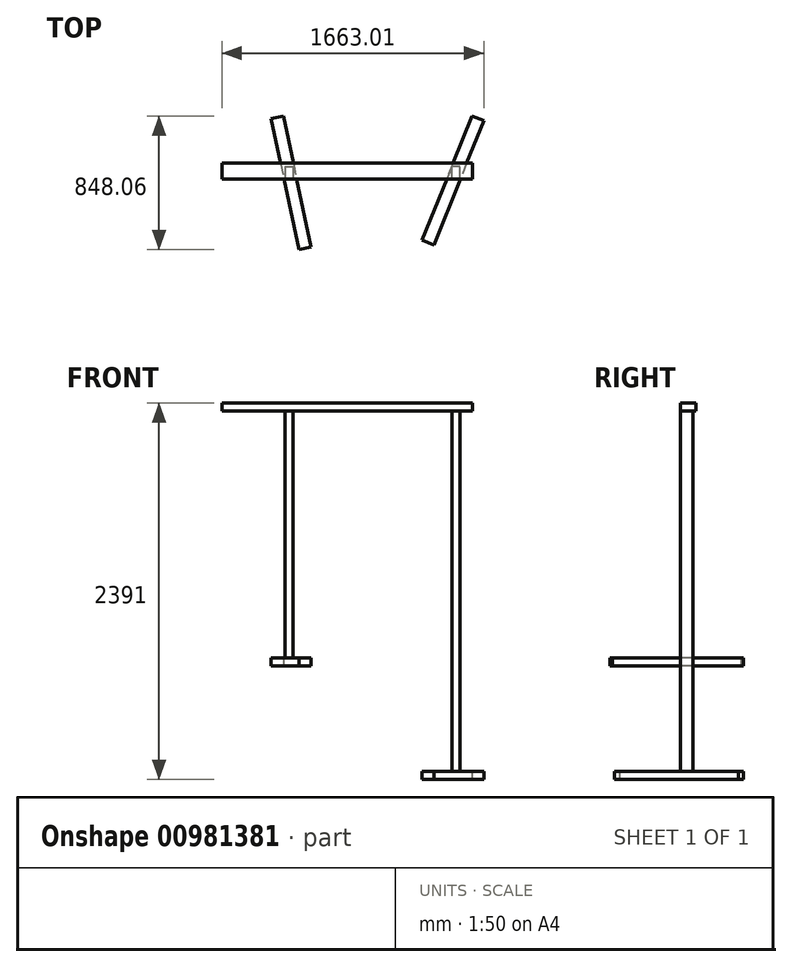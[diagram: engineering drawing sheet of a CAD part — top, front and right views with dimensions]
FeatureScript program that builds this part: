
annotation { "Feature Type Name" : "Feature", "Feature Type Description" : "" }
export const myFeature = defineFeature(function(context is Context, id is Id, definition is map)
    precondition{}
    {
        {
            var Q0;
            Q0=qCreatedBy(makeId("Top.planeOp"),FACE);
            var sketch = newSketch(context, id + "F0", { "sketchPlane" : qUnion([Q0])});
            skLineSegment(sketch, "E0.bottom", {"start": v(-104.92, 429.48) * mm, "end": v(-26.67, 446.11) * mm});
            skLineSegment(sketch, "E0.top", {"start": v(71.8, -401.95) * mm, "end": v(150.05, -385.31) * mm});
            skLineSegment(sketch, "E0.left", {"start": v(-104.92, 429.48) * mm, "end": v(71.8, -401.95) * mm});
            skLineSegment(sketch, "E0.right", {"start": v(-26.67, 446.11) * mm, "end": v(150.05, -385.31) * mm});
            skLineSegment(sketch, "E1.bottom", {"start": v(1173.33, 446.11) * mm, "end": v(1247.5, 416.14) * mm});
            skLineSegment(sketch, "E1.top", {"start": v(854.91, -342) * mm, "end": v(929.09, -371.96) * mm});
            skLineSegment(sketch, "E1.left", {"start": v(1173.33, 446.11) * mm, "end": v(854.91, -342) * mm});
            skLineSegment(sketch, "E1.right", {"start": v(1247.5, 416.14) * mm, "end": v(929.09, -371.96) * mm});
            skSolve(sketch);
        }
        {
            var Q0;
            Q0=makeQuery(id+"F0.imprint","IMPRINT",FACE,{"disambiguationData":[TD([[makeQuery(id+"F0.imprint","IMPRINT",EDGE,{"derivedFrom":sQuery(id+"F0.wireOp",EDGE,"E0.bottom")}),-1.0]])]});
            var Q1;
            Q1=makeQuery(id+"F0.imprint","IMPRINT",FACE,{"disambiguationData":[TD([[makeQuery(id+"F0.imprint","IMPRINT",EDGE,{"derivedFrom":sQuery(id+"F0.wireOp",EDGE,"E1.bottom")}),-1.0]])]});
            extrude(context, id + "F1", {"entities" : qUnion([Q0, Q1]), "depth" : 50 * mm, "offsetDistance" : 25 * mm});
        }
        {
            var Q0;
            Q0=qCreatedBy(makeId("Front.planeOp"),FACE);
            var sketch = newSketch(context, id + "F2", { "sketchPlane" : qUnion([Q0])});
            skLineSegment(sketch, "E2", {"start": v(-1961.24, -1265) * mm, "end": v(3128.52, -1265) * mm});
            skLineSegment(sketch, "E3", {"start": v(-1961.24, -722) * mm, "end": v(3128.52, -722) * mm});
            skLineSegment(sketch, "E4", {"start": v(-1961.24, 0) * mm, "end": v(3203.88, 0) * mm});
            skLineSegment(sketch, "E5", {"start": v(-1961.24, 1630.83) * mm, "end": v(3320.54, 1630.83) * mm});
            skLineSegment(sketch, "E6", {"start": v(-1961.24, 1176.34) * mm, "end": v(-1961.24, -1253.17) * mm});
            skSolve(sketch);
        }
        {
            var Q0;
            Q0=makeQuery(id+"F1.opExtrude","SWEPT_BODY",BODY,{"disambiguationData":[OSD([sQuery(id+"F0.wireOp",EDGE,"E1.bottom"),sQuery(id+"F0.wireOp",EDGE,"E1.top"),sQuery(id+"F0.wireOp",EDGE,"E1.left"),sQuery(id+"F0.wireOp",EDGE,"E1.right")])]});
            var Q1;
            Q1=sQuery(id+"F2.wireOp",EDGE,"E6");
            transform(context, id + "F3", {"entities" : qUnion([Q0]), "transformType" : TransformType.TRANSLATION_DISTANCE, "transformDirection" : qUnion([Q1]), "distance" : 722 * mm, "makeCopy" : false});
        }
        {
            var Q0;
            Q0=qCreatedBy(makeId("Right.planeOp"),FACE);
            var sketch = newSketch(context, id + "F4", { "sketchPlane" : qUnion([Q0])});
            skLineSegment(sketch, "E7.bottom", {"start": v(46.11, -672) * mm, "end": v(126.11, -672) * mm});
            skLineSegment(sketch, "E7.top", {"start": v(46.11, 1619) * mm, "end": v(126.11, 1619) * mm});
            skLineSegment(sketch, "E7.left", {"start": v(46.11, -672) * mm, "end": v(46.11, 1619) * mm});
            skLineSegment(sketch, "E7.right", {"start": v(126.11, -672) * mm, "end": v(126.11, 1619) * mm});
            skSolve(sketch);
        }
        {
            var Q0;
            Q0=makeQuery(id+"F4.imprint","IMPRINT",FACE,{"disambiguationData":[TD([[makeQuery(id+"F4.imprint","IMPRINT",EDGE,{"derivedFrom":sQuery(id+"F4.wireOp",EDGE,"E7.bottom")}),1.0]])]});
            extrude(context, id + "F5", {"entities" : qUnion([Q0]), "depth" : 50 * mm, "offsetDistance" : 25 * mm});
        }
        {
            var Q0;
            Q0=makeQuery(id+"F5.opExtrude","SWEPT_BODY",BODY,{"disambiguationData":[OSD([sQuery(id+"F4.wireOp",EDGE,"E7.bottom"),sQuery(id+"F4.wireOp",EDGE,"E7.top"),sQuery(id+"F4.wireOp",EDGE,"E7.left"),sQuery(id+"F4.wireOp",EDGE,"E7.right")])]});
            var Q1;
            Q1=makeQuery(id+"F5.opExtrude","SWEPT_EDGE",EDGE,{"disambiguationData":[OSD([sQuery(id+"F4.wireOp",EDGE,"E7.bottom"),sQuery(id+"F4.wireOp",EDGE,"E7.right")])]});
            transform(context, id + "F6", {"entities" : qUnion([Q0]), "transformType" : TransformType.TRANSLATION_DISTANCE, "transformDirection" : qUnion([Q1]), "distance" : 1046 * mm, "oppositeDirection" : true, "makeCopy" : false});
        }
        {
            var Q0;
            Q0=makeQuery(id+"F1.opExtrude","CAP_FACE",FACE,{"disambiguationData":[OSD([sQuery(id+"F0.wireOp",EDGE,"E0.bottom"),sQuery(id+"F0.wireOp",EDGE,"E0.top"),sQuery(id+"F0.wireOp",EDGE,"E0.left"),sQuery(id+"F0.wireOp",EDGE,"E0.right")])],"isStart":false});
            var sketch = newSketch(context, id + "F7", { "sketchPlane" : qUnion([Q0])});
            skLineSegment(sketch, "E8.bottom", {"start": v(-15.51, 126.11) * mm, "end": v(34.49, 126.11) * mm});
            skLineSegment(sketch, "E8.top", {"start": v(-15.51, 46.11) * mm, "end": v(34.49, 46.11) * mm});
            skLineSegment(sketch, "E8.left", {"start": v(-15.51, 126.11) * mm, "end": v(-15.51, 46.11) * mm});
            skLineSegment(sketch, "E8.right", {"start": v(34.49, 126.11) * mm, "end": v(34.49, 46.11) * mm});
            skSolve(sketch);
        }
        {
            var Q0;
            Q0=makeQuery(id+"F7.imprint","IMPRINT",FACE,{"disambiguationData":[TD([[makeQuery(id+"F7.imprint","IMPRINT",EDGE,{"derivedFrom":sQuery(id+"F7.wireOp",EDGE,"E8.bottom")}),-1.0]])]});
            extrude(context, id + "F8", {"entities" : qUnion([Q0]), "depth" : 1569 * mm, "offsetDistance" : 25 * mm});
        }
        {
            var Q0;
            Q0=makeQuery(id+"F8.opExtrude","SWEPT_FACE",FACE,{"disambiguationData":[OSD([sQuery(id+"F7.wireOp",EDGE,"E8.top")])]});
            var sketch = newSketch(context, id + "F9", { "sketchPlane" : qUnion([Q0])});
            skLineSegment(sketch, "E9.bottom", {"start": v(-415.51, 1619) * mm, "end": v(1176, 1619) * mm});
            skLineSegment(sketch, "E9.top", {"start": v(-415.51, 1669) * mm, "end": v(1176, 1669) * mm});
            skLineSegment(sketch, "E9.left", {"start": v(-415.51, 1619) * mm, "end": v(-415.51, 1669) * mm});
            skLineSegment(sketch, "E9.right", {"start": v(1176, 1619) * mm, "end": v(1176, 1669) * mm});
            skSolve(sketch);
        }
        {
            var Q0;
            Q0=makeQuery(id+"F9.imprint","IMPRINT",FACE,{"disambiguationData":[TD([[makeQuery(id+"F9.imprint","IMPRINT",EDGE,{"derivedFrom":sQuery(id+"F9.wireOp",EDGE,"E9.top")}),-1.0]])]});
            extrude(context, id + "F10", {"entities" : qUnion([Q0]), "oppositeDirection" : true, "depth" : 100 * mm, "offsetDistance" : 25 * mm});
        }
    });
